# Revit family: Bidet_Two-Handle-American_Standard-Colony_Soft-3475.501
name_source: partatom
category: Plumbing Fixtures
revit_build: Autodesk Revit 2014 (Build: 20130308_1515(x64)
units: mm (PartAtom-declared; Revit-internal decimal feet)

## types (1)
- 3475.501
    ADA Compliant = Yes
    Assembly Code = D2020300
    CW Connection = Yes
    CWFU = 1.5
    Default Elevation = 0"
    Description = Colony Soft Fixture-Mounted Bidet Fitting
    HW Connection = Yes
    HWFU = 1.5
    Height = 7"
    Length = 4 7/8"
    Manufacturer = American Standard
    Material = Metal-American Standard-002-Polished Chrome
    Model = 3475.501
    Price = Prices may vary. Please consult Manufacturer Representative for most up-to-date price list.
    Product Documentation Link = https://www.americanstandard-us.com
    Product Page URL = http://www.americanstandard-us.com
    Revised Date = 01/23/2017
    Specification = Fixture-Mounted Bidet Fitting. Vacuum breaker. Metal Speed Connect Pop-up drain. Metal lever handles.
    URL = http://www.americanstandard-us.com
    Vent Connection = No
    WFU = 2
    Warranty Information = Faucet Lifetime Function, Commercial Application (5 Years).
    Waste Connection = No
    Width = 13 3/4"

## geometry (parser evidence)
native form markers: Sweep x1
no freeform markers — native parametric forms only
